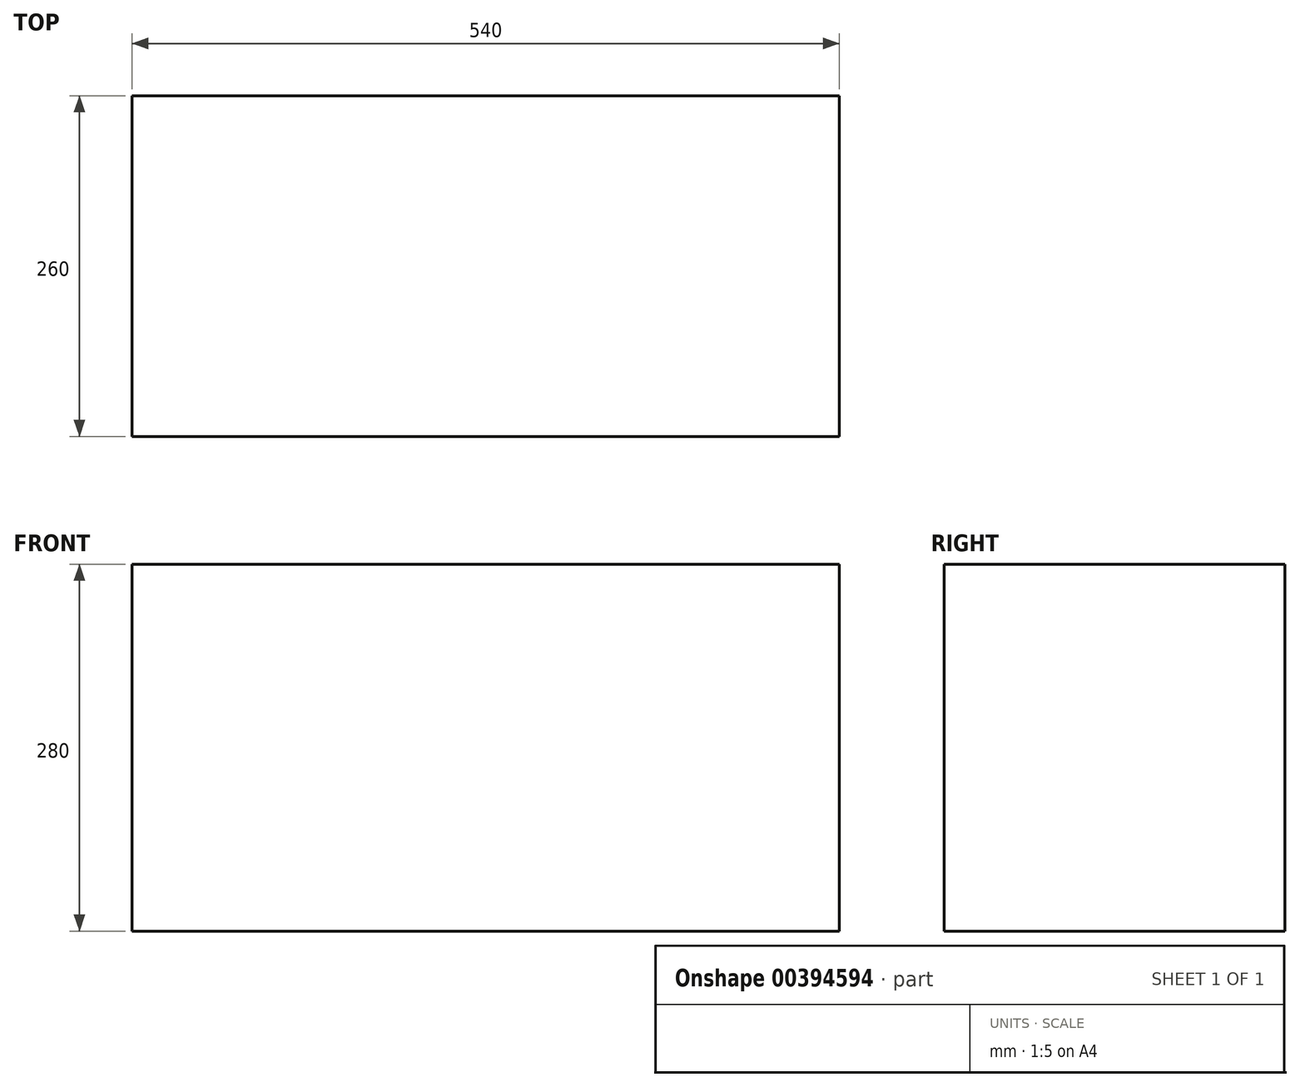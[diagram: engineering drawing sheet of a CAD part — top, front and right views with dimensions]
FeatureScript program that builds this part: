
annotation { "Feature Type Name" : "Feature", "Feature Type Description" : "" }
export const myFeature = defineFeature(function(context is Context, id is Id, definition is map)
    precondition{}
    {
        {
            var Q0;
            Q0=qCreatedBy(makeId("Top.planeOp"),FACE);
            var sketch = newSketch(context, id + "F0", { "sketchPlane" : qUnion([Q0])});
            skLineSegment(sketch, "E0.bottom", {"start": v(270, -130) * mm, "end": v(-270, -130) * mm});
            skLineSegment(sketch, "E0.top", {"start": v(270, 130) * mm, "end": v(-270, 130) * mm});
            skLineSegment(sketch, "E0.left", {"start": v(270, -130) * mm, "end": v(270, 130) * mm});
            skLineSegment(sketch, "E0.right", {"start": v(-270, -130) * mm, "end": v(-270, 130) * mm});
            skPoint(sketch, "E0.middle", {"position": v(0, 0) * mm});
            skSolve(sketch);
        }
        {
            var Q0;
            Q0=makeQuery(id+"F0.imprint","IMPRINT",FACE,{"disambiguationData":[TD([[makeQuery(id+"F0.imprint","IMPRINT",EDGE,{"derivedFrom":sQuery(id+"F0.wireOp",EDGE,"E0.bottom")}),-1.0]])]});
            extrude(context, id + "F1", {"entities" : qUnion([Q0]), "depth" : 280 * mm});
        }
    });
